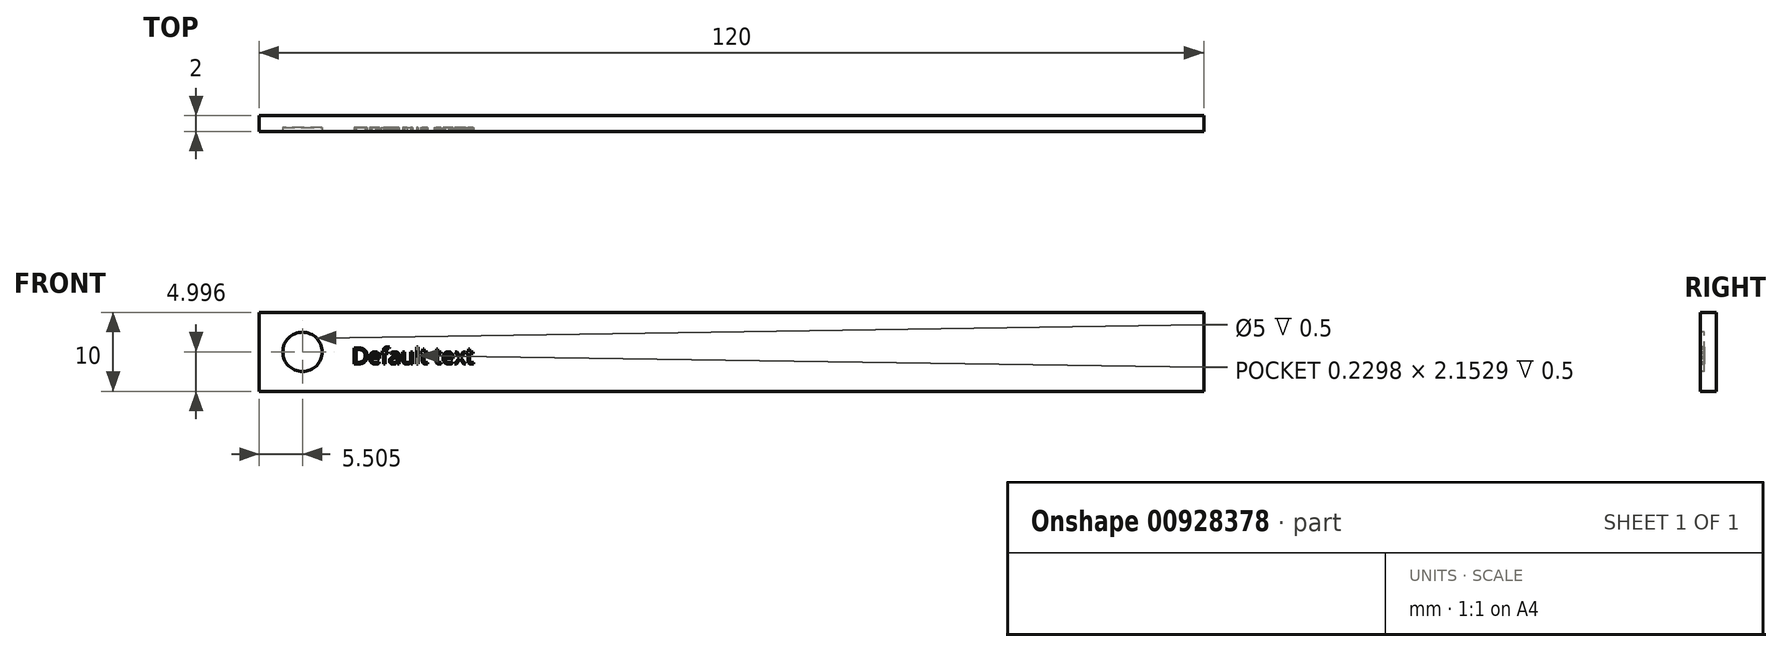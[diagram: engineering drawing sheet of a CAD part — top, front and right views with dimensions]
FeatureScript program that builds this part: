
annotation { "Feature Type Name" : "Feature", "Feature Type Description" : "" }
export const myFeature = defineFeature(function(context is Context, id is Id, definition is map)
    precondition{}
    {
        {
            var Q0;
            Q0=qCreatedBy(makeId("Front.planeOp"),FACE);
            var sketch = newSketch(context, id + "F0", { "sketchPlane" : qUnion([Q0])});
            skLineSegment(sketch, "E0.bottom", {"start": v(-55.17, -11) * mm, "end": v(64.83, -11) * mm});
            skLineSegment(sketch, "E0.top", {"start": v(-55.17, -1) * mm, "end": v(64.83, -1) * mm});
            skLineSegment(sketch, "E0.left", {"start": v(-55.17, -11) * mm, "end": v(-55.17, -1) * mm});
            skLineSegment(sketch, "E0.right", {"start": v(64.83, -11) * mm, "end": v(64.83, -1) * mm});
            skSolve(sketch);
        }
        {
            var Q0;
            Q0=makeQuery(id+"F0.imprint","IMPRINT",FACE,{"disambiguationData":[TD([[makeQuery(id+"F0.imprint","IMPRINT",EDGE,{"derivedFrom":sQuery(id+"F0.wireOp",EDGE,"E0.bottom")}),1.0]])]});
            var sketch = newSketch(context, id + "F1", { "sketchPlane" : qUnion([Q0])});
            skSolve(sketch);
        }
        {
            var Q0;
            Q0=makeQuery(id+"F1.imprint","IMPRINT",FACE,{"disambiguationData":[TD([[makeQuery(id+"F1.imprint","IMPRINT",EDGE,{"derivedFrom":makeQuery(id+"F0.imprint","IMPRINT",EDGE,{"derivedFrom":sQuery(id+"F0.wireOp",EDGE,"E0.bottom")})}),1.0]])]});
            extrude(context, id + "F2", {"entities" : qUnion([Q0]), "depth" : 2 * mm, "offsetDistance" : 25 * mm});
        }
        {
            var Q0;
            Q0=makeQuery(id+"F2.opExtrude","CAP_FACE",FACE,{"disambiguationData":[OSD([sQuery(id+"F0.wireOp",EDGE,"E0.bottom"),sQuery(id+"F0.wireOp",EDGE,"E0.top"),sQuery(id+"F0.wireOp",EDGE,"E0.left"),sQuery(id+"F0.wireOp",EDGE,"E0.right")])],"isStart":false});
            var sketch = newSketch(context, id + "F3", { "sketchPlane" : qUnion([Q0])});
            skCircle(sketch, "E1", {"center": v(-49.67, -6) * mm, "radius": 2.5 * mm});
            skText(sketch, "E2", { "text": "Default text", "fontName": "OpenSans-Regular.ttf"});
            const initialGuessF3  = {"E2": [-0.04336, -0.00752, 1, 0, 0.00204]};
            skSetInitialGuess(sketch, initialGuessF3);
            skSolve(sketch);
        }
        {
            var Q0;
            Q0 = qSketchRegion(id + "F3", true);
            extrude(context, id + "F4", {"entities" : qUnion([Q0]), "operationType" : NewBodyOperationType.REMOVE, "oppositeDirection" : true, "depth" : 0.5 * mm, "offsetDistance" : 25 * mm});
        }
    });
